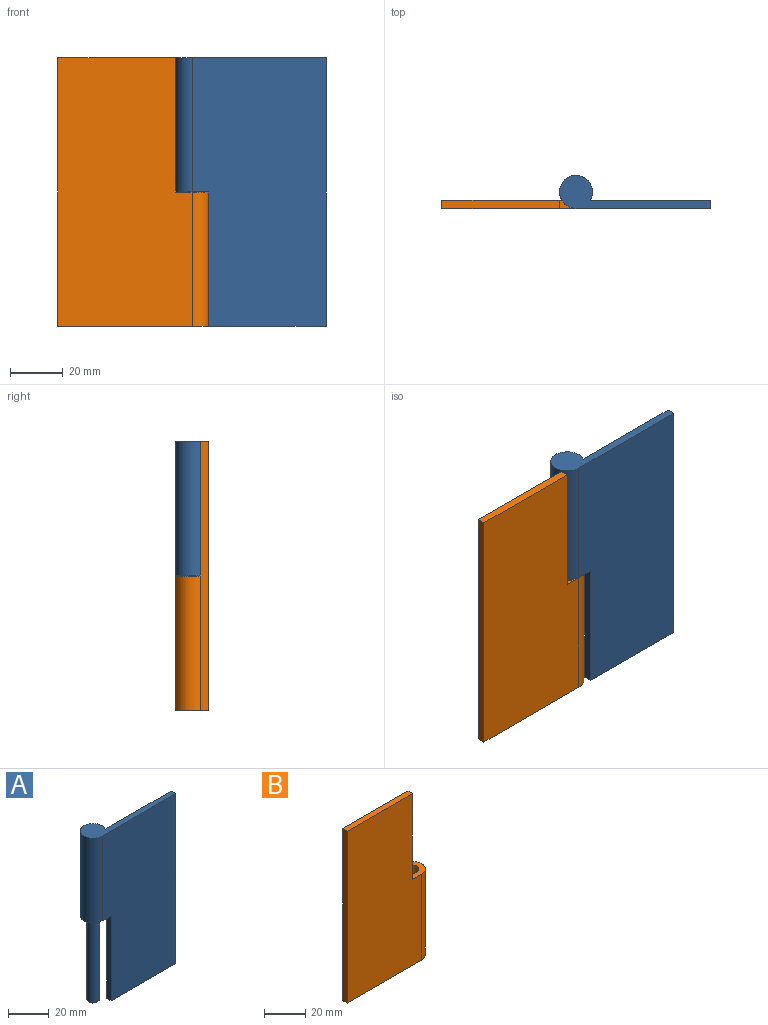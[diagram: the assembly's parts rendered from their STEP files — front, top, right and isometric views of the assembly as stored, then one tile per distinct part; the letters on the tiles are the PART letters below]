
ASSEMBLY  parts=2 mates=1
PART A: 11 faces, bbox 57x12.4x101.6 mm
  f0: plane 12.45x12.45mm, normal (0,0,-1), area 97.4mm2, adj f1,f2,f3,f7,f8
  f1: cylinder r=6.22mm len=50.8mm, axis (0,0,1), area 1659mm2, adj f0,f2,f3,f6
  f2: plane 101.6x45.45mm, normal (0,1,0), area 4573.3mm2, adj f0,f1,f4,f5,f6,f7
  f3: plane 101.6x50.8mm, normal (0,-1,0), area 4845.2mm2, adj f0,f1,f4,f5,f6,f7
  f4: plane 44.58x3.05mm, normal (0,0,-1), area 135.9mm2, adj f2,f3,f5,f7
  f5: plane 101.6x3.05mm, normal (1,0,0), area 309.7mm2, adj f2,f3,f4,f6
  f6: plane 57.02x12.45mm, normal (0,0,1), area 264.9mm2, adj f1,f2,f3,f5
  f7: plane 50.8x3.05mm, normal (-1,0,0), area 154.8mm2, adj f0,f2,f3,f4
  f8: cylinder r=3.17mm len=49.53mm, axis (0,0,1), area 988.1mm2, adj f0,f9
  f9: cone r=3.17mm half-angle=45deg, axis (0,0,1), area 28.7mm2, adj f8,f10
  f10: plane 3.81x3.81mm, normal (0,0,-1), area 11.4mm2, adj f9
PART B: 10 faces, bbox 57x12.4x101.6 mm
  f0: plane 101.6x50.8mm, normal (0,1,0), area 4845.2mm2, adj f1,f5,f6,f7,f8,f9
  f1: cylinder r=3.17mm len=50.8mm, axis (0,0,1), area 860.4mm2, adj f0,f2,f7,f8
  f2: plane 50.8x2.79mm, normal (0.42,-0.91,0), area 156.2mm2, adj f1,f3,f7,f8
  f3: cylinder r=6.22mm len=50.8mm, axis (0,0,1), area 1657.5mm2, adj f2,f4,f7,f8
  f4: plane 101.6x50.8mm, normal (0,-1,0), area 4845.2mm2, adj f3,f5,f6,f7,f8,f9
  f5: plane 44.58x3.05mm, normal (0,0,1), area 135.9mm2, adj f0,f4,f6,f9
  f6: plane 101.6x3.05mm, normal (-1,0,0), area 309.7mm2, adj f0,f4,f5,f7
  f7: plane 57.02x12.45mm, normal (0,0,-1), area 230.4mm2, adj f0,f1,f2,f3,f4,f6
  f8: plane 12.45x12.45mm, normal (0,0,1), area 94.5mm2, adj f0,f1,f2,f3,f4,f9
  f9: plane 50.8x3.05mm, normal (1,0,0), area 154.8mm2, adj f0,f4,f5,f8
PLACE A rot(axis=(1,0,0),0deg) t=(0,0,0)mm
PLACE B at identity
MATE revolute A.f1 <-> B.f1  axis (0,0,-1) through (0,6.22,-50.8)mm
